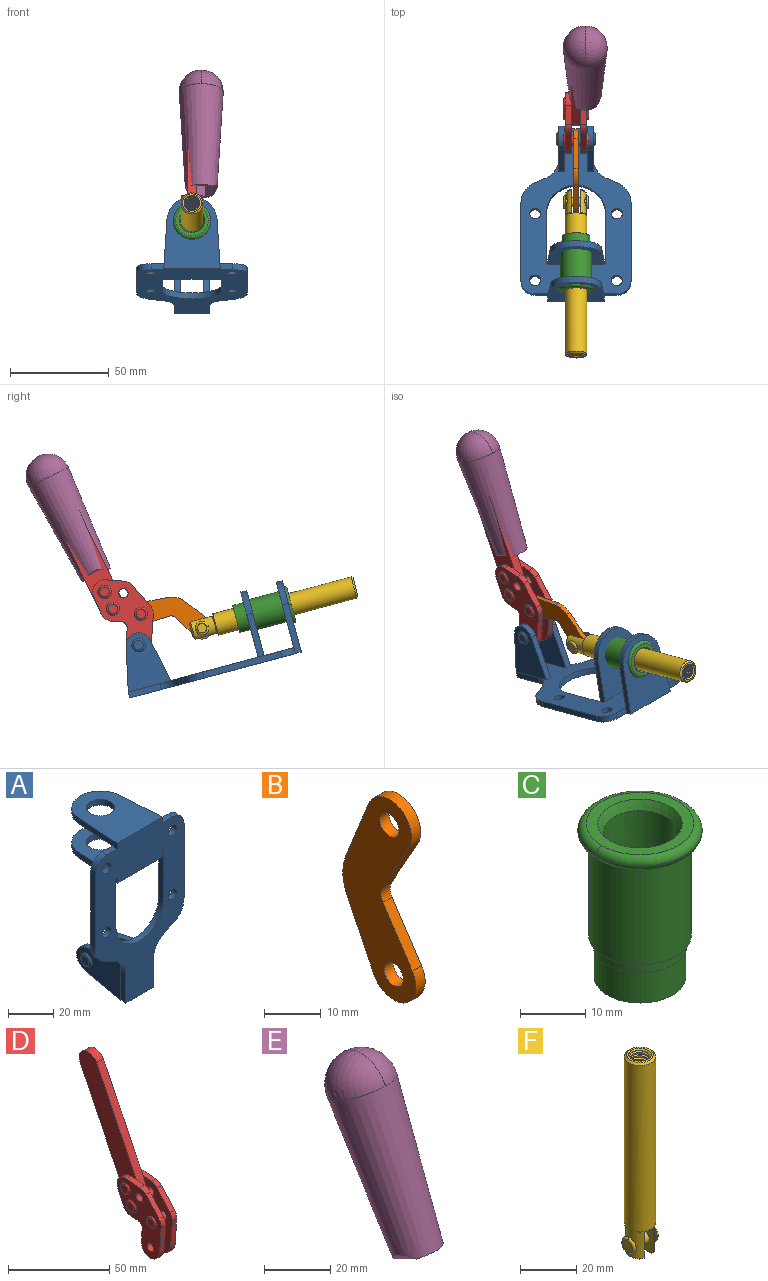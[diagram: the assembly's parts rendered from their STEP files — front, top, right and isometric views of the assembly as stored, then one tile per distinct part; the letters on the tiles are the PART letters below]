
ASSEMBLY  parts=6 mates=6
PART A: 55 faces, bbox 55.7x37.4x89.8 mm
  f0: torus R=2.41mm, axis (-1,0,0), area 15mm2, adj f11,f15,f25
  f1: torus R=2.41mm, axis (-1,0,0), area 15mm2, adj f10,f12,f22
  f2: cylinder r=2.78mm len=5.56mm, axis (0,-1,0), area 54.2mm2, adj f30,f54
  f3: cylinder r=14.99mm len=29.97mm, axis (0,-1,0), area 145.9mm2, adj f30,f49,f53,f54
  f4: cylinder r=2.78mm len=5.56mm, axis (0,-1,0), area 54.2mm2, adj f30,f54
  f5: cylinder r=2.78mm len=5.56mm, axis (0,-1,0), area 54.2mm2, adj f30,f54
  f6: cylinder r=2.78mm len=5.56mm, axis (0,-1,0), area 54.2mm2, adj f30,f54
  f7: cylinder r=6.35mm len=12.7mm, axis (0,0,1), area 123.6mm2, adj f27,f51
  f8: cylinder r=6.35mm len=12.7mm, axis (0,0,-1), area 124.7mm2, adj f21,f35
  f9: cylinder r=2.41mm len=11.18mm, axis (-1,0,0), area 169.4mm2, adj f16,f19
  f10: plane 4.83x4.83mm, normal (1,0,0), area 18.3mm2, adj f1,f12
  f11: plane 4.83x4.83mm, normal (-1,0,0), area 18.3mm2, adj f0,f15
  f12: torus R=2.41mm, axis (-1,0,0), area 15mm2, adj f1,f10,f22
  f13: cylinder r=6.35mm len=12.41mm, axis (1,0,0), area 53.4mm2, adj f18,f19,f22,f23
  f14: cylinder r=6.35mm len=12.41mm, axis (-1,0,0), area 53.4mm2, adj f16,f17,f24,f25
  f15: torus R=2.41mm, axis (-1,0,0), area 15mm2, adj f0,f11,f25
  f16: plane 27.86x22.35mm, normal (1,0,0), area 425.4mm2, adj f9,f14,f17,f24,f30
  f17: plane 22.86x4.97mm, normal (0,0.21,0.98), area 72.5mm2, adj f14,f16,f25,f30
  f18: plane 22.86x4.97mm, normal (0,0.21,0.98), area 72.5mm2, adj f13,f19,f22,f30
  f19: plane 27.86x22.35mm, normal (-1,0,0), area 425.4mm2, adj f9,f13,f18,f23,f30
  f20: cylinder r=12.7mm len=25.35mm, axis (0,0,-1), area 119.8mm2, adj f21,f34,f35,f36
  f21: plane 34.21x28.07mm, normal (0,0,-1), area 702.4mm2, adj f8,f20,f30,f34,f36
  f22: plane 27.96x22.45mm, normal (1,0,0), area 407.2mm2, adj f1,f12,f13,f18,f23,f30,f42,f43
  f23: plane 22.86x4.97mm, normal (0,0.21,-0.98), area 72.5mm2, adj f13,f19,f22,f44
  f24: plane 22.86x4.97mm, normal (0,0.21,-0.98), area 72.5mm2, adj f14,f16,f25,f44
  f25: plane 27.86x22.35mm, normal (-1,0,0), area 407.1mm2, adj f0,f14,f15,f17,f24,f30,f45,f46
  f26: plane 3.1x0.95mm, normal (0,0,-1), area 2.7mm2, adj f30,f49,f50,f54
  f27: plane 34.21x28.07mm, normal (0,0,1), area 702.4mm2, adj f7,f28,f30,f50,f52
  f28: cylinder r=12.7mm len=25.35mm, axis (0,0,1), area 118.8mm2, adj f27,f50,f51,f52
  f29: plane 3.1x0.95mm, normal (0,0,-1), area 2.7mm2, adj f30,f52,f53,f54
  f30: plane 86.54x55.63mm, normal (0,1,0), area 2362.9mm2, adj f2,f3,f4,f5,f6,f16,f17,f18
  f31: plane 40.56x3.1mm, normal (-1,0,0), area 125.7mm2, adj f30,f32,f48,f54
  f32: cylinder r=7.11mm len=7.11mm, axis (0,-1,0), area 34.6mm2, adj f30,f31,f33,f54
  f33: plane 6.67x3.1mm, normal (0,0,1), area 20.4mm2, adj f30,f32,f34,f54
  f34: plane 25.39x3.13mm, normal (-1,0.06,0), area 79.5mm2, adj f20,f21,f33,f35,f54
  f35: plane 37.31x28.45mm, normal (0,0,1), area 789.9mm2, adj f8,f20,f34,f36,f54
  f36: plane 25.39x3.13mm, normal (1,0.06,0), area 79.5mm2, adj f20,f21,f35,f37,f54
  f37: plane 6.67x3.1mm, normal (0,0,1), area 20.4mm2, adj f30,f36,f38,f54
  f38: cylinder r=7.11mm len=7.11mm, axis (0,-1,0), area 34.6mm2, adj f30,f37,f39,f54
  f39: plane 40.56x3.1mm, normal (1,0,0), area 125.7mm2, adj f30,f38,f40,f54
  f40: cylinder r=11.18mm len=10.16mm, axis (0,-1,0), area 39.5mm2, adj f30,f39,f41,f54
  f41: plane 6.09x3.1mm, normal (0.42,0,-0.91), area 20.8mm2, adj f30,f40,f42,f54
  f42: cylinder r=11.18mm len=9.41mm, axis (0,-1,0), area 37.2mm2, adj f22,f30,f41,f43,f54
  f43: plane 16.5x3.1mm, normal (1,0,0), area 51.1mm2, adj f22,f42,f44,f54
  f44: plane 17.37x3.1mm, normal (0,0,-1), area 53.8mm2, adj f23,f24,f30,f43,f45,f54
  f45: plane 16.5x3.1mm, normal (-1,0,0), area 51.1mm2, adj f25,f44,f46,f54
  f46: cylinder r=11.18mm len=9.41mm, axis (0,-1,0), area 37.2mm2, adj f25,f30,f45,f47,f54
  f47: plane 6.09x3.1mm, normal (-0.42,0,-0.91), area 20.8mm2, adj f30,f46,f48,f54
  f48: cylinder r=11.18mm len=10.16mm, axis (0,-1,0), area 39.5mm2, adj f30,f31,f47,f54
  f49: plane 26.54x3.1mm, normal (-1,0,0), area 82.3mm2, adj f3,f26,f30,f54
  f50: plane 25.39x3.1mm, normal (1,0.06,0), area 78.8mm2, adj f26,f27,f28,f51,f54
  f51: plane 37.31x28.45mm, normal (0,0,-1), area 789.9mm2, adj f7,f28,f50,f52,f54
  f52: plane 25.39x3.1mm, normal (-1,0.06,0), area 78.8mm2, adj f27,f28,f29,f51,f54
  f53: plane 26.54x3.1mm, normal (1,0,0), area 82.3mm2, adj f3,f29,f30,f54
  f54: plane 89.66x55.63mm, normal (0,-1,0), area 2678.5mm2, adj f2,f3,f4,f5,f6,f26,f29,f31
PART B: 12 faces, bbox 2.3x18.2x42.8 mm
  f0: cylinder r=2.4mm len=4.8mm, axis (1,0,0), area 34.9mm2, adj f4,f11
  f1: cylinder r=10.41mm len=8.47mm, axis (1,0,0), area 20.2mm2, adj f4,f9,f10,f11
  f2: cylinder r=3.05mm len=3.16mm, axis (1,0,0), area 7.7mm2, adj f4,f6,f7,f11
  f3: cylinder r=2.4mm len=4.8mm, axis (1,0,0), area 34.9mm2, adj f4,f11
  f4: plane 42.81x18.23mm, normal (-1,0,0), area 414.1mm2, adj f0,f1,f2,f3,f5,f6,f7,f8
  f5: cylinder r=5.54mm len=10.67mm, axis (1,0,0), area 41.8mm2, adj f4,f6,f10,f11
  f6: plane 11.66x6.53mm, normal (0,-0.87,-0.49), area 30.9mm2, adj f2,f4,f5,f11
  f7: plane 11.17x7.33mm, normal (0,-0.84,0.55), area 30.9mm2, adj f2,f4,f8,f11
  f8: cylinder r=5.54mm len=10.51mm, axis (1,0,0), area 41.8mm2, adj f4,f7,f9,f11
  f9: plane 13.67x6.67mm, normal (0,0.9,-0.44), area 35.1mm2, adj f1,f4,f8,f11
  f10: plane 14.1x5.7mm, normal (0,0.93,0.37), area 35.1mm2, adj f1,f4,f5,f11
  f11: plane 42.81x18.23mm, normal (1,0,0), area 414.1mm2, adj f0,f1,f2,f3,f5,f6,f7,f8
PART C: 15 faces, bbox 20.6x20.6x28.7 mm
  f0: torus R=8.26mm, axis (0,0,1), area 56.8mm2, adj f1,f10,f12
  f1: torus R=8.26mm, axis (0,0,1), area 56.8mm2, adj f0,f6,f13
  f2: cylinder r=5.59mm len=25.91mm, axis (0,0,1), area 909.6mm2, adj f3,f4
  f3: cone r=6.86mm half-angle=45deg, axis (0,0,-1), area 70.2mm2, adj f2,f14
  f4: cone r=6.47mm half-angle=30deg, axis (0,0,1), area 66.7mm2, adj f2,f13
  f5: cylinder r=7.04mm len=14.07mm, axis (0,0,1), area 252.6mm2, adj f11,f14
  f6: torus R=8.26mm, axis (0,0,1), area 56.8mm2, adj f1,f12,f13
  f7: cylinder r=7.16mm len=14.33mm, axis (0,0,1), area 91.5mm2, adj f9,f11
  f8: cylinder r=7.86mm len=18.42mm, axis (0,0,1), area 909.6mm2, adj f9,f10
  f9: plane 15.72x15.72mm, normal (0,0,-1), area 33mm2, adj f7,f8
  f10: plane 16.51x16.51mm, normal (0,0,-1), area 19.9mm2, adj f0,f8,f12
  f11: plane 14.33x14.33mm, normal (0,0,-1), area 5.7mm2, adj f5,f7
  f12: torus R=8.26mm, axis (0,0,1), area 56.8mm2, adj f0,f6,f10
  f13: plane 16.51x16.51mm, normal (0,0,1), area 82.7mm2, adj f1,f4,f6
  f14: plane 14.07x14.07mm, normal (0,0,-1), area 7.8mm2, adj f3,f5
PART D: 59 faces, bbox 12.9x60.2x99.6 mm
  f0: torus R=2.39mm, axis (-1,0,0), area 14.9mm2, adj f20,f43,f51
  f1: torus R=2.39mm, axis (-1,0,0), area 14.9mm2, adj f19,f42,f51
  f2: torus R=2.39mm, axis (-1,0,0), area 14.9mm2, adj f18,f35,f51
  f3: torus R=2.39mm, axis (-1,0,0), area 14.9mm2, adj f14,f17,f23
  f4: torus R=2.39mm, axis (-1,0,0), area 14.9mm2, adj f13,f16,f23
  f5: torus R=2.39mm, axis (-1,0,0), area 14.9mm2, adj f12,f15,f23
  f6: cylinder r=2.39mm len=4.78mm, axis (1,0,0), area 46.5mm2, adj f48,f50,f51
  f7: cylinder r=2.39mm len=4.78mm, axis (1,0,0), area 46.5mm2, adj f50,f51
  f8: cylinder r=6.35mm len=12.68mm, axis (1,0,0), area 61.8mm2, adj f38,f39,f50,f51
  f9: cylinder r=2.39mm len=4.78mm, axis (-1,0,0), area 70.5mm2, adj f46,f50
  f10: cylinder r=2.39mm len=4.78mm, axis (-1,0,0), area 46.5mm2, adj f23,f45,f46
  f11: cylinder r=2.39mm len=4.78mm, axis (-1,0,0), area 46.5mm2, adj f23,f46
  f12: plane 4.78x4.78mm, normal (1,0,0), area 17.9mm2, adj f5,f15
  f13: plane 4.78x4.78mm, normal (1,0,0), area 17.9mm2, adj f4,f16
  f14: plane 4.78x4.78mm, normal (1,0,0), area 17.9mm2, adj f3,f17
  f15: torus R=2.39mm, axis (-1,0,0), area 14.9mm2, adj f5,f12,f23
  f16: torus R=2.39mm, axis (-1,0,0), area 14.9mm2, adj f4,f13,f23
  f17: torus R=2.39mm, axis (-1,0,0), area 14.9mm2, adj f3,f14,f23
  f18: plane 4.78x4.78mm, normal (-1,0,0), area 17.9mm2, adj f2,f35
  f19: plane 4.78x4.78mm, normal (-1,0,0), area 17.9mm2, adj f1,f42
  f20: plane 4.78x4.78mm, normal (-1,0,0), area 17.9mm2, adj f0,f43
  f21: plane 2.26x0.2mm, normal (1,0,0), area 0.2mm2, adj f31,f44
  f22: plane 2.26x0.2mm, normal (-1,0,0), area 0.2mm2, adj f41,f44
  f23: plane 39.37x30.77mm, normal (1,0,0), area 565.5mm2, adj f3,f4,f5,f10,f11,f15,f16,f17
  f24: cylinder r=6.1mm len=4.15mm, axis (-1,0,0), area 14.7mm2, adj f23,f25,f32,f46
  f25: plane 10.25x9.01mm, normal (0,-0.75,0.66), area 42.3mm2, adj f23,f24,f26,f46
  f26: cylinder r=6.35mm len=4.64mm, axis (-1,0,0), area 15.6mm2, adj f23,f25,f27,f46
  f27: plane 15.84x3.1mm, normal (0,-1,-0.07), area 49.2mm2, adj f23,f26,f28,f46
  f28: cylinder r=6.35mm len=12.68mm, axis (-1,0,0), area 61.8mm2, adj f23,f27,f29,f46
  f29: plane 8.11x3.1mm, normal (0,1,0.07), area 25.2mm2, adj f23,f28,f30,f46
  f30: cylinder r=3.05mm len=3.25mm, axis (-1,0,0), area 14.8mm2, adj f23,f29,f31,f46
  f31: plane 5.99x3.1mm, normal (0,0.07,-1), area 18.6mm2, adj f21,f23,f30,f44,f46
  f32: plane 9.5x3.1mm, normal (0,-0.07,1), area 29.5mm2, adj f23,f24,f33,f46,f47
  f33: cylinder r=6.1mm len=8.63mm, axis (-1,0,0), area 39.1mm2, adj f23,f32,f34,f47
  f34: plane 8.65x3.96mm, normal (0,0.91,-0.42), area 29.5mm2, adj f23,f33,f44,f47
  f35: torus R=2.39mm, axis (-1,0,0), area 14.9mm2, adj f2,f18,f51
  f36: plane 10.25x9.01mm, normal (0,-0.75,0.66), area 42.3mm2, adj f37,f49,f50,f51
  f37: cylinder r=6.35mm len=4.64mm, axis (1,0,0), area 15.6mm2, adj f36,f38,f50,f51
  f38: plane 15.84x3.1mm, normal (0,-1,-0.07), area 49.2mm2, adj f8,f37,f50,f51
  f39: plane 8.11x3.1mm, normal (0,1,0.07), area 25.2mm2, adj f8,f40,f50,f51
  f40: cylinder r=3.05mm len=3.25mm, axis (1,0,0), area 14.8mm2, adj f39,f41,f50,f51
  f41: plane 5.99x3.1mm, normal (0,0.07,-1), area 18.6mm2, adj f22,f40,f44,f50,f51
  f42: torus R=2.39mm, axis (-1,0,0), area 14.9mm2, adj f1,f19,f51
  f43: torus R=2.39mm, axis (-1,0,0), area 14.9mm2, adj f0,f20,f51
  f44: cylinder r=6.35mm len=12.12mm, axis (-1,0,0), area 128.9mm2, adj f21,f22,f23,f31,f34,f41,f46,f47
  f45: plane 2.65x1.35mm, normal (1,0,0), area 1mm2, adj f10,f55
  f46: plane 39.08x20.42mm, normal (-1,0,0), area 412.5mm2, adj f9,f10,f11,f24,f25,f26,f27,f28
  f47: plane 77.62x39.82mm, normal (1,0,0), area 850mm2, adj f32,f33,f34,f44,f53,f54,f55
  f48: plane 2.65x1.35mm, normal (-1,0,0), area 1mm2, adj f6,f55
  f49: cylinder r=6.1mm len=4.15mm, axis (1,0,0), area 14.7mm2, adj f36,f50,f51,f56
  f50: plane 39.08x20.42mm, normal (1,0,0), area 412.5mm2, adj f6,f7,f8,f9,f36,f37,f38,f39
  f51: plane 39.37x30.77mm, normal (-1,0,0), area 565.5mm2, adj f0,f1,f2,f6,f7,f8,f35,f36
  f52: plane 8.65x3.96mm, normal (0,0.91,-0.42), area 29.5mm2, adj f44,f51,f57,f58
  f53: plane 68.49x33.4mm, normal (0,0.9,-0.44), area 358.1mm2, adj f44,f47,f54,f58
  f54: cylinder r=6.35mm len=12.06mm, axis (1,0,0), area 93.7mm2, adj f47,f53,f55,f58
  f55: plane 68.49x33.4mm, normal (0,-0.9,0.44), area 358.1mm2, adj f44,f45,f46,f47,f48,f50,f54,f58
  f56: plane 9.5x3.1mm, normal (0,-0.07,1), area 29.5mm2, adj f49,f50,f51,f57,f58
  f57: cylinder r=6.1mm len=8.63mm, axis (1,0,0), area 39.1mm2, adj f51,f52,f56,f58
  f58: plane 77.62x39.82mm, normal (-1,0,0), area 850mm2, adj f44,f52,f53,f54,f55,f56,f57
PART E: 11 faces, bbox 22.3x42.6x64.5 mm
  f0: sphere r=11.13mm, area 411.4mm2, adj f1,f8
  f1: cone r=11.11mm half-angle=3.3deg, axis (0,0.44,0.9), area 3251.8mm2, adj f0,f7,f8,f9,f10
  f2: cylinder r=6.16mm len=11.7mm, axis (1,0,0), area 89.5mm2, adj f3,f4,f5,f6
  f3: plane 60.23x36.75mm, normal (-1,0,0), area 763.6mm2, adj f2,f4,f6,f10
  f4: plane 51.37x25.05mm, normal (0,0.9,-0.44), area 264.2mm2, adj f2,f3,f5,f10
  f5: plane 60.23x36.75mm, normal (1,0,0), area 763.6mm2, adj f2,f4,f6,f10
  f6: plane 51.37x25.05mm, normal (0,-0.9,0.44), area 264.2mm2, adj f2,f3,f5,f10
  f7: plane 9.95x5.95mm, normal (0.71,-0.31,-0.64), area 25.8mm2, adj f1,f10
  f8: sphere r=11.13mm, area 411.4mm2, adj f0,f1
  f9: plane 9.95x5.95mm, normal (-0.71,-0.31,-0.64), area 25.8mm2, adj f1,f10
  f10: plane 14.27x11.38mm, normal (0,-0.44,-0.9), area 106.7mm2, adj f1,f3,f4,f5,f6,f7,f9
PART F: 48 faces, bbox 12.6x11.1x86.1 mm
  f0: torus R=2.41mm, axis (-1,0,0), area 15mm2, adj f30,f32,f34
  f1: torus R=2.41mm, axis (-1,0,0), area 15mm2, adj f29,f31,f33
  f2: cylinder r=5.54mm len=72.39mm, axis (0,0,1), area 2518.5mm2, adj f3,f4,f42,f43
  f3: cone r=5.54mm half-angle=45deg, axis (0,0,1), area 7.6mm2, adj f2,f5,f41
  f4: cone r=5.54mm half-angle=45deg, axis (0,0,-1), area 34.9mm2, adj f2,f39
  f5: cylinder r=5.08mm len=11.48mm, axis (0,0,1), area 108.3mm2, adj f3,f7,f8,f41
  f6: cylinder r=2.41mm len=4.83mm, axis (-1,0,0), area 71.2mm2, adj f40,f41
  f7: cylinder r=2.41mm len=4.83mm, axis (-1,0,0), area 7.6mm2, adj f5,f34
  f8: cone r=5.08mm half-angle=45deg, axis (0,0,1), area 10.6mm2, adj f5,f37,f41
  f9: cone r=3.98mm half-angle=45deg, axis (0,0,1), area 17.6mm2, adj f27,f39,f45,f46,f47
  f10: cylinder r=2.41mm len=4.83mm, axis (-1,0,0), area 7.6mm2, adj f33,f38
  f11: cylinder r=3.2mm len=6.4mm, axis (0,0,1), area 78.4mm2, adj f12,f28,f44,f45,f47
  f12: cylinder r=3.2mm len=6.4mm, axis (0,0,1), area 10.5mm2, adj f11,f13,f45,f47
  f13: cylinder r=3.2mm len=6.4mm, axis (0,0,1), area 10.5mm2, adj f12,f14,f45,f47
  f14: cylinder r=3.2mm len=6.4mm, axis (0,0,1), area 10.5mm2, adj f13,f15,f45,f47
  f15: cylinder r=3.2mm len=6.4mm, axis (0,0,1), area 10.5mm2, adj f14,f16,f45,f47
  f16: cylinder r=3.2mm len=6.4mm, axis (0,0,1), area 10.5mm2, adj f15,f17,f45,f47
  f17: cylinder r=3.2mm len=6.4mm, axis (0,0,1), area 10.5mm2, adj f16,f18,f45,f47
  f18: cylinder r=3.2mm len=6.4mm, axis (0,0,1), area 10.5mm2, adj f17,f19,f45,f47
  f19: cylinder r=3.2mm len=6.4mm, axis (0,0,1), area 10.5mm2, adj f18,f20,f45,f47
  f20: cylinder r=3.2mm len=6.4mm, axis (0,0,1), area 10.5mm2, adj f19,f21,f45,f47
  f21: cylinder r=3.2mm len=6.4mm, axis (0,0,1), area 10.5mm2, adj f20,f22,f45,f47
  f22: cylinder r=3.2mm len=6.4mm, axis (0,0,1), area 10.5mm2, adj f21,f23,f45,f47
  f23: cylinder r=3.2mm len=6.4mm, axis (0,0,1), area 10.5mm2, adj f22,f24,f45,f47
  f24: cylinder r=3.2mm len=6.4mm, axis (0,0,1), area 10.5mm2, adj f23,f25,f45,f47
  f25: cylinder r=3.2mm len=6.4mm, axis (0,0,1), area 10.5mm2, adj f24,f26,f45,f47
  f26: cylinder r=3.2mm len=6.4mm, axis (0,0,1), area 10.5mm2, adj f25,f27,f45,f47
  f27: cylinder r=3.2mm len=6.4mm, axis (0,0,1), area 7.4mm2, adj f9,f26,f45,f47
  f28: cone r=3.2mm half-angle=60deg, axis (0,0,1), area 37.2mm2, adj f11
  f29: plane 4.83x4.83mm, normal (-1,0,0), area 18.3mm2, adj f1,f31
  f30: plane 4.83x4.83mm, normal (1,0,0), area 18.3mm2, adj f0,f32
  f31: torus R=2.41mm, axis (-1,0,0), area 15mm2, adj f1,f29,f33
  f32: torus R=2.41mm, axis (-1,0,0), area 15mm2, adj f0,f30,f34
  f33: plane 6.83x6.83mm, normal (1,0,0), area 18.3mm2, adj f1,f10,f31
  f34: plane 6.83x6.83mm, normal (-1,0,0), area 18.3mm2, adj f0,f7,f32
  f35: cone r=5.08mm half-angle=45deg, axis (0,0,1), area 10.6mm2, adj f36,f38,f40
  f36: plane 7.25x1.97mm, normal (0,0,-1), area 10mm2, adj f35,f40
  f37: plane 7.25x1.97mm, normal (0,0,-1), area 10mm2, adj f8,f41
  f38: cylinder r=5.08mm len=11.48mm, axis (0,0,1), area 108.3mm2, adj f10,f35,f40,f42
  f39: plane 9.55x9.55mm, normal (0,0,1), area 22mm2, adj f4,f9
  f40: plane 12.76x10.09mm, normal (1,0,0), area 95.7mm2, adj f6,f35,f36,f38,f42,f43
  f41: plane 12.76x10.09mm, normal (-1,0,0), area 95.7mm2, adj f3,f5,f6,f8,f37,f43
  f42: cone r=5.54mm half-angle=45deg, axis (0,0,1), area 7.6mm2, adj f2,f38,f40
  f43: plane 11.07x4.7mm, normal (0,0,-1), area 50.4mm2, adj f2,f40,f41
  f44: plane 0.89x0.62mm, normal (-1,0,0), area 0.3mm2, adj f11,f45,f46,f47
  f45: bspline ~24.8x7.63mm, area 266.6mm2, adj f9,f11,f12,f13,f14,f15,f16,f17
  f46: bspline ~24.87x7.63mm, area 73.6mm2, adj f9,f44,f45,f47
  f47: bspline ~24.98x7.63mm, area 272.5mm2, adj f9,f11,f12,f13,f14,f15,f16,f17
PLACE A rot(axis=(1,0,0),75deg) t=(-1.31,15.5,1.47)mm
PLACE B rot(axis=(1,0,0),105.2deg) t=(-1.31,42.25,5.82)mm
PLACE C rot(axis=(1,0,0),75deg) t=(-1.31,16.73,1.14)mm
PLACE D t=(-1.31,28.26,49.03)mm
PLACE E t=(3.35,28.26,49.03)mm
PLACE F rot(axis=(1,0,0),75deg) t=(-1.31,29.43,-2.27)mm
MATE fastened D.f54 <-> E.f2  axis (1,0,0) through (1.04,99.3,103.8)mm
MATE slider F.f2 <-> C.f2  axis (0,-0.97,0.26) through (-1.31,-20.97,36.72)mm
MATE fastened C.f2 <-> A.f7  axis (0,-0.97,0.26) through (-1.31,-22.94,37.25)mm
MATE revolute D.f7 <-> A.f0  axis (-1,0,0) through (-1.31,52.87,16.93)mm
MATE revolute B.f5 <-> F.f6  axis (1,0,0) through (-1.31,20.86,25.51)mm
MATE revolute B.f3 <-> D.f4  axis (1,0,0) through (-1.31,51.77,32.77)mm
